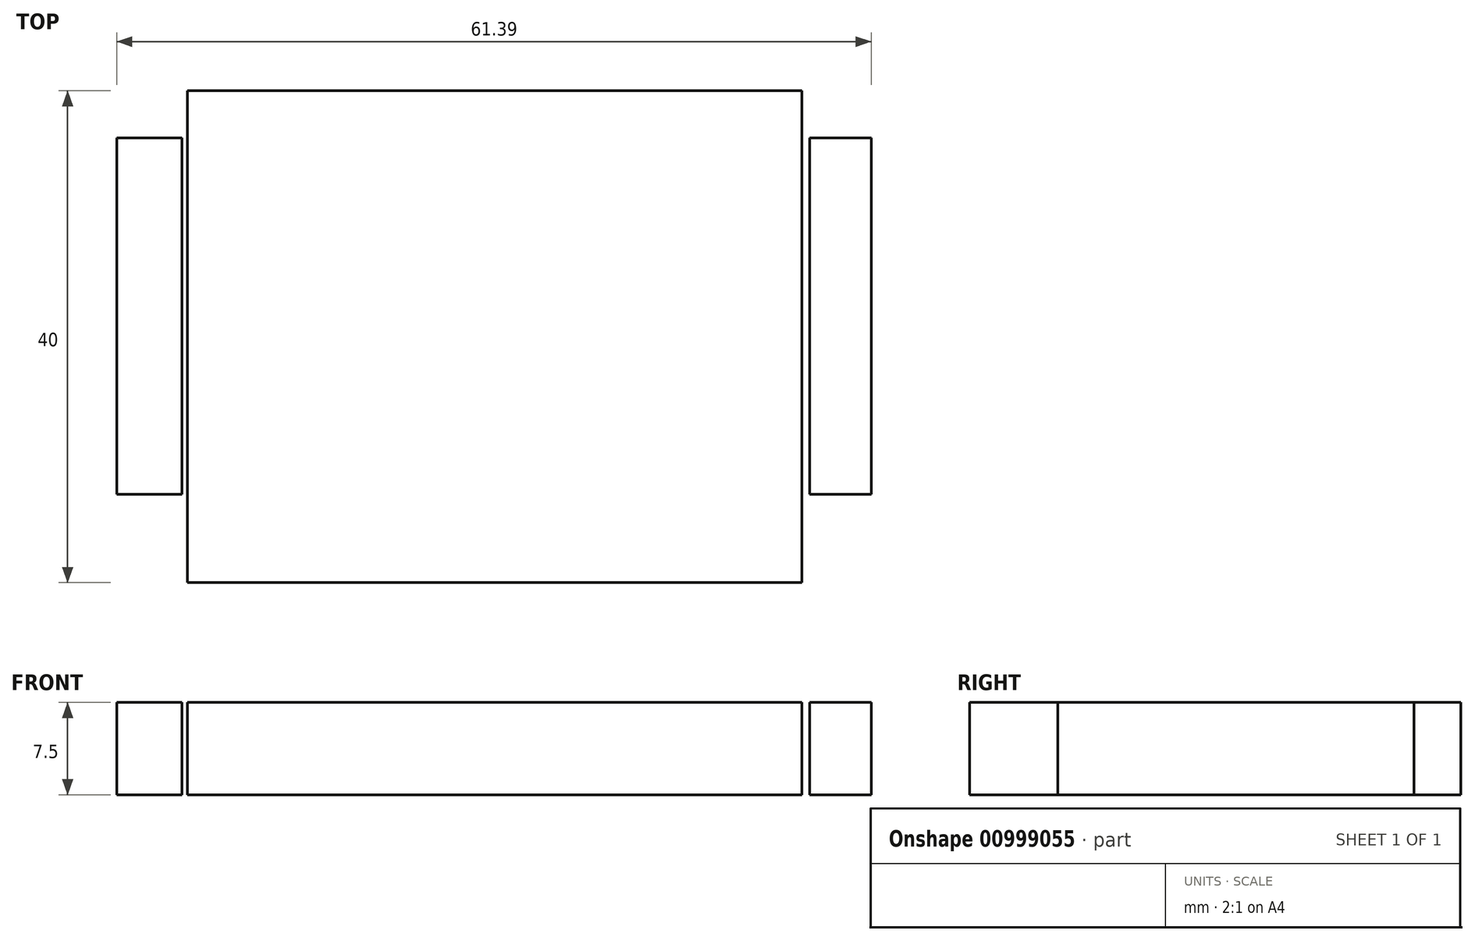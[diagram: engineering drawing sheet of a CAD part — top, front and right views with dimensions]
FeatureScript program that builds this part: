
annotation { "Feature Type Name" : "Feature", "Feature Type Description" : "" }
export const myFeature = defineFeature(function(context is Context, id is Id, definition is map)
    precondition{}
    {
        {
            var Q0;
            Q0=qCreatedBy(makeId("Top.planeOp"),FACE);
            var sketch = newSketch(context, id + "F0", { "sketchPlane" : qUnion([Q0])});
            skLineSegment(sketch, "E0.bottom", {"start": v(25, 20) * mm, "end": v(-25, 20) * mm});
            skLineSegment(sketch, "E0.top", {"start": v(25, -20) * mm, "end": v(-25, -20) * mm});
            skLineSegment(sketch, "E0.left", {"start": v(25, 20) * mm, "end": v(25, -20) * mm});
            skLineSegment(sketch, "E0.right", {"start": v(-25, 20) * mm, "end": v(-25, -20) * mm});
            skPoint(sketch, "E0.middle", {"position": v(0, 0) * mm});
            skSolve(sketch);
        }
        {
            var Q0;
            Q0=makeQuery(id+"F0.imprint","IMPRINT",FACE,{"disambiguationData":[TD([[makeQuery(id+"F0.imprint","IMPRINT",EDGE,{"derivedFrom":sQuery(id+"F0.wireOp",EDGE,"E0.bottom")}),1.0]])]});
            extrude(context, id + "F1", {"entities" : qUnion([Q0]), "depth" : 7.5 * mm, "offsetDistance" : 25 * mm});
        }
        {
            var Q0;
            Q0=qCreatedBy(makeId("Top.planeOp"),FACE);
            var sketch = newSketch(context, id + "F2", { "sketchPlane" : qUnion([Q0])});
            skLineSegment(sketch, "E1", {"start": v(25.64, 16.19) * mm, "end": v(30.64, 16.19) * mm, "construction": true});
            skLineSegment(sketch, "E2", {"start": v(25.64, -12.81) * mm, "end": v(30.64, -12.81) * mm, "construction": true});
            skLineSegment(sketch, "E3.bottom", {"start": v(25.64, 16.19) * mm, "end": v(30.64, 16.19) * mm});
            skLineSegment(sketch, "E3.top", {"start": v(25.64, -12.81) * mm, "end": v(30.64, -12.81) * mm});
            skLineSegment(sketch, "E3.left", {"start": v(25.64, 16.19) * mm, "end": v(25.64, -12.81) * mm});
            skLineSegment(sketch, "E3.right", {"start": v(30.64, 16.19) * mm, "end": v(30.64, -12.81) * mm});
            skLineSegment(sketch, "E4", {"start": v(-25.45, 16.19) * mm, "end": v(-30.75, 16.19) * mm});
            skLineSegment(sketch, "E5", {"start": v(-25.45, -12.81) * mm, "end": v(-30.75, -12.81) * mm});
            skLineSegment(sketch, "E6.left", {"start": v(-25.45, -12.81) * mm, "end": v(-25.45, 16.19) * mm});
            skLineSegment(sketch, "E6.right", {"start": v(-30.75, -12.81) * mm, "end": v(-30.75, 16.19) * mm});
            skPoint(sketch, "E7.orphan", {"position": v(-45.22, -12.81) * mm});
            skSolve(sketch);
        }
        {
            var Q0;
            Q0=makeQuery(id+"F2.imprint","IMPRINT",FACE,{"disambiguationData":[TD([[makeQuery(id+"F2.imprint","IMPRINT",EDGE,{"derivedFrom":sQuery(id+"F2.wireOp",EDGE,"E4")}),1.0]])]});
            var Q1;
            Q1=makeQuery(id+"F2.imprint","IMPRINT",FACE,{"disambiguationData":[TD([[makeQuery(id+"F2.imprint","IMPRINT",EDGE,{"derivedFrom":sQuery(id+"F2.wireOp",EDGE,"E3.bottom")}),-1.0]])]});
            extrude(context, id + "F3", {"entities" : qUnion([Q0, Q1]), "depth" : 7.5 * mm, "offsetDistance" : 25 * mm});
        }
    });
